# Revit family: ПУМ_30.06.2021
name_source: partatom
category: Оборудование
units: mm (PartAtom-declared; Revit-internal decimal feet)

## family parameters
Всегда вертикально = Да
Классификация = Нет
На основе рабочей плоскости = Нет
Общий = Нет
При загрузке вырезать с полостями = Нет
Размер круглого соединителя = Использовать диаметр
Тип детали = Нормальный
Точка расчета площади = Нет

## types (2) — shared parameters
светодиод RS-PUM = Нет
светодиод Питание = Нет
текст RS-PR для ПР-10.5 = Нет
текст RS-PUM = Нет
текст ПР-10.5 = Нет
текст ПР-4.2 = Нет
текст Питание = Нет
текст Прибор расширения = Нет
текст Работа = Нет
zero-valued in all types: Отметка по умолчанию

## per-type parameters (varying)
| type | Панель | светодиод RS-485 | светодиод RS-PR | светодиод Прибор | текст RS-485 | текст RS-PR | текст ПУМ | текст ПУМ 4.2 | текст Прибор |
| Прибор управления малый модификации 4.2 | Нет | Да | Да | Да | Да | Да | Нет | Да | Да |
| Прибор управления малый | Да | Нет | Нет | Нет | Нет | Нет | Да | Нет | Нет |
